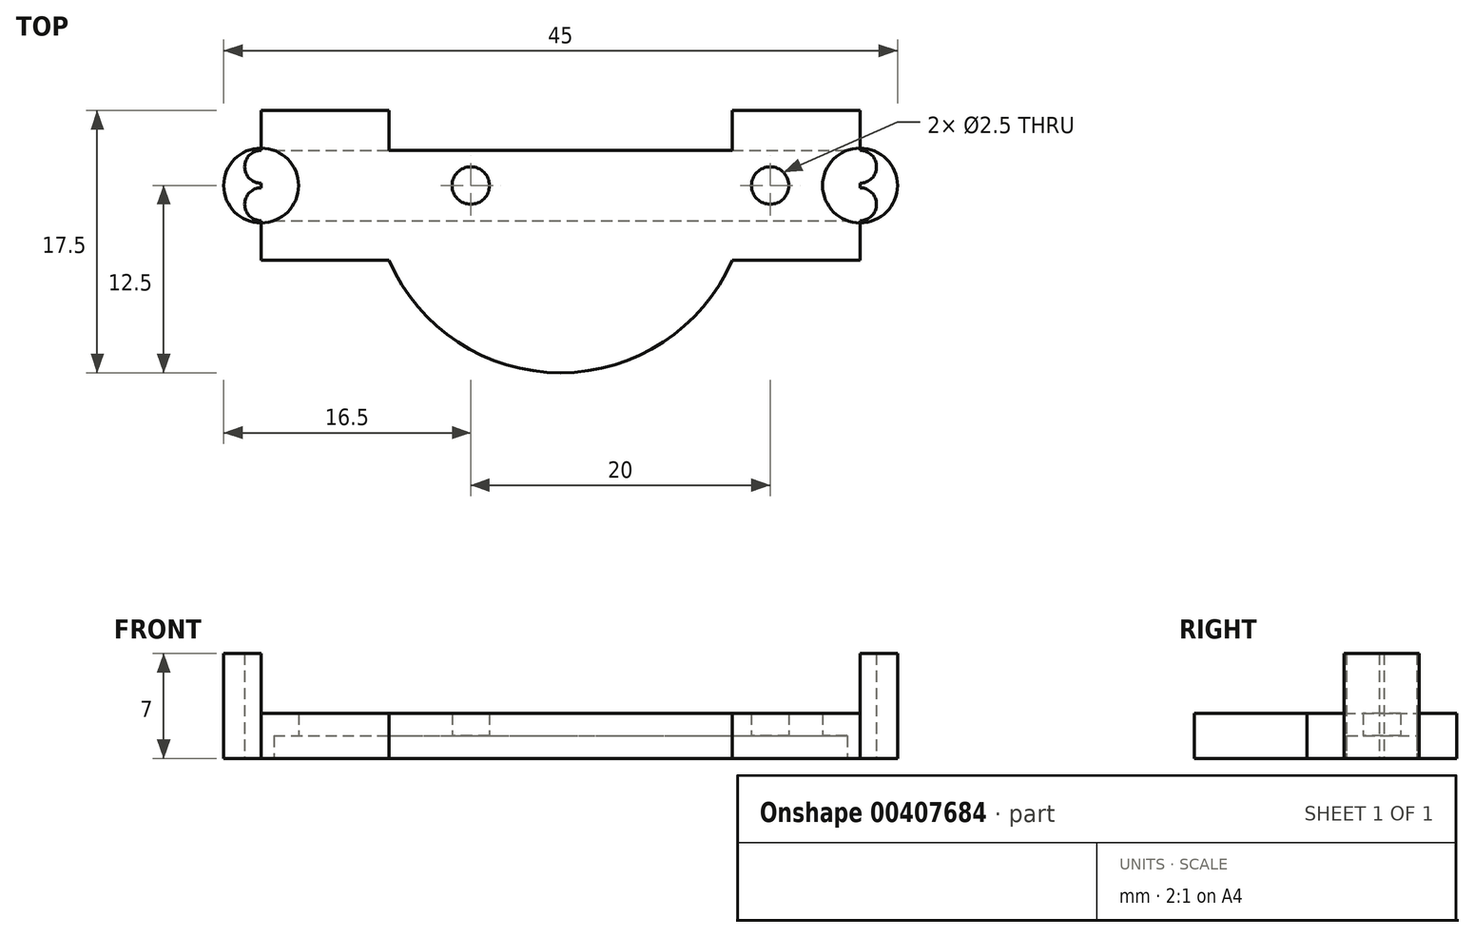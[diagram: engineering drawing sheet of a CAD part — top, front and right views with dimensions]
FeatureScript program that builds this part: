
annotation { "Feature Type Name" : "Feature", "Feature Type Description" : "" }
export const myFeature = defineFeature(function(context is Context, id is Id, definition is map)
    precondition{}
    {
        {
            var Q0;
            Q0=qCreatedBy(makeId("Top.planeOp"),FACE);
            var sketch = newSketch(context, id + "F0", { "sketchPlane" : qUnion([Q0])});
            skCircle(sketch, "E0", {"center": v(0, 0) * mm, "radius": 12.5 * mm});
            skCircle(sketch, "E1", {"center": v(-20, 0) * mm, "radius": 5 * mm});
            skCircle(sketch, "E2", {"center": v(20, 0) * mm, "radius": 5 * mm});
            skLineSegment(sketch, "E3.bottom", {"start": v(-20, 5) * mm, "end": v(-11.46, 5) * mm});
            skLineSegment(sketch, "E3.top", {"start": v(-20, -5) * mm, "end": v(-11.46, -5) * mm});
            skLineSegment(sketch, "E3.left", {"start": v(-20, 5) * mm, "end": v(-20, -5) * mm});
            skLineSegment(sketch, "E3.right", {"start": v(-11.46, 5) * mm, "end": v(-11.46, -5) * mm});
            skLineSegment(sketch, "E4.bottom", {"start": v(20, 5) * mm, "end": v(11.46, 5) * mm});
            skLineSegment(sketch, "E4.top", {"start": v(20, -5) * mm, "end": v(11.46, -5) * mm});
            skLineSegment(sketch, "E4.left", {"start": v(20, 5) * mm, "end": v(20, -5) * mm});
            skLineSegment(sketch, "E4.right", {"start": v(11.46, 5) * mm, "end": v(11.46, -5) * mm});
            skCircle(sketch, "E5", {"center": v(-20, -1.25) * mm, "radius": 1.1 * mm});
            skCircle(sketch, "E6", {"center": v(0, 0) * mm, "radius": 11.5 * mm});
            skPoint(sketch, "E7.firstSnap0", {"position": v(0, -2.27) * mm});
            skCircle(sketch, "E8", {"center": v(-6, 0) * mm, "radius": 1.25 * mm});
            skCircle(sketch, "E9", {"center": v(14, 0) * mm, "radius": 1.25 * mm});
            skCircle(sketch, "E10", {"center": v(-20, 1.25) * mm, "radius": 1.1 * mm});
            skCircle(sketch, "E11", {"center": v(20, -1.25) * mm, "radius": 1.1 * mm});
            skCircle(sketch, "E12", {"center": v(20, 1.25) * mm, "radius": 1.1 * mm});
            skLineSegment(sketch, "E13.bottom", {"start": v(-20, 2.35) * mm, "end": v(20, 2.35) * mm});
            skLineSegment(sketch, "E13.top", {"start": v(-20, -2.35) * mm, "end": v(20, -2.35) * mm});
            skLineSegment(sketch, "E13.left", {"start": v(-20, 2.35) * mm, "end": v(-20, -2.35) * mm});
            skLineSegment(sketch, "E13.right", {"start": v(20, 2.35) * mm, "end": v(20, -2.35) * mm});
            skCircle(sketch, "E14", {"center": v(-20, 0) * mm, "radius": 2.5 * mm});
            skCircle(sketch, "E15", {"center": v(20, 0) * mm, "radius": 2.5 * mm});
            skSolve(sketch);
        }
        {
            var Q0;
            {var subQ1=sQuery(id+"F0.wireOp",EDGE,"E13.bottom");var subQ5=sQuery(id+"F0.wireOp",EDGE,"E1");var subQ6=makeQuery(id+"F0.imprint","INTERSECT",VERTEX,{"derivedFrom":[subQ5,subQ1]});Q0=makeQuery(id+"F0.imprint","IMPRINT",FACE,{"disambiguationData":[TD([[makeQuery(id+"F0.imprint","IMPRINT",EDGE,{"disambiguationData":[TD([[subQ6,1.0]])],"derivedFrom":subQ5}),1.0]])]});}
            var Q1;
            {var subQ1=sQuery(id+"F0.wireOp",EDGE,"E1");var subQ3=sQuery(id+"F0.wireOp",EDGE,"E13.top");var subQ4=makeQuery(id+"F0.imprint","INTERSECT",VERTEX,{"derivedFrom":[subQ1,subQ3]});Q1=makeQuery(id+"F0.imprint","IMPRINT",FACE,{"disambiguationData":[TD([[makeQuery(id+"F0.imprint","IMPRINT",EDGE,{"disambiguationData":[TD([[subQ4,1.0]])],"derivedFrom":subQ1}),1.0]])]});}
            var Q2;
            {var subQ1=sQuery(id+"F0.wireOp",EDGE,"E1");var subQ3=sQuery(id+"F0.wireOp",EDGE,"E13.bottom");var subQ4=makeQuery(id+"F0.imprint","INTERSECT",VERTEX,{"derivedFrom":[subQ1,subQ3]});Q2=makeQuery(id+"F0.imprint","IMPRINT",FACE,{"disambiguationData":[TD([[makeQuery(id+"F0.imprint","IMPRINT",EDGE,{"disambiguationData":[TD([[subQ4,-1.0]])],"derivedFrom":subQ1}),1.0]])]});}
            var Q3;
            {var subQ3=sQuery(id+"F0.wireOp",EDGE,"E13.left");var subQ6=sQuery(id+"F0.wireOp",EDGE,"E5");var subQ8=makeQuery(id+"F0.imprint","INTERSECT",VERTEX,{"derivedFrom":[subQ6,subQ3]});Q3=makeQuery(id+"F0.imprint","IMPRINT",FACE,{"disambiguationData":[TD([[makeQuery(id+"F0.imprint","IMPRINT",EDGE,{"disambiguationData":[TD([[subQ8,1.0]])],"derivedFrom":subQ3}),-1.0]])]});}
            var Q4;
            {var subQ0=sQuery(id+"F0.wireOp",EDGE,"E3.bottom");Q4=makeQuery(id+"F0.imprint","IMPRINT",FACE,{"disambiguationData":[TD([[makeQuery(id+"F0.imprint","IMPRINT",EDGE,{"derivedFrom":subQ0}),-1.0]])]});}
            var Q5;
            {var subQ0=sQuery(id+"F0.wireOp",EDGE,"E3.top");Q5=makeQuery(id+"F0.imprint","IMPRINT",FACE,{"disambiguationData":[TD([[makeQuery(id+"F0.imprint","IMPRINT",EDGE,{"derivedFrom":subQ0}),1.0]])]});}
            var Q6;
            {var subQ0=sQuery(id+"F0.wireOp",EDGE,"E13.bottom");var subQ1=sQuery(id+"F0.wireOp",EDGE,"E0");var subQ2=makeQuery(id+"F0.imprint","INTERSECT",VERTEX,{"disambiguationData":[OD(1.0)],"derivedFrom":[subQ1,subQ0]});Q6=makeQuery(id+"F0.imprint","IMPRINT",FACE,{"disambiguationData":[TD([[makeQuery(id+"F0.imprint","IMPRINT",EDGE,{"disambiguationData":[TD([[subQ2,-1.0]])],"derivedFrom":subQ1}),-1.0]])]});}
            var Q7;
            {var subQ1=sQuery(id+"F0.wireOp",EDGE,"E0");var subQ3=sQuery(id+"F0.wireOp",EDGE,"E13.bottom");var subQ4=makeQuery(id+"F0.imprint","INTERSECT",VERTEX,{"disambiguationData":[OD(1.0)],"derivedFrom":[subQ1,subQ3]});Q7=makeQuery(id+"F0.imprint","IMPRINT",FACE,{"disambiguationData":[TD([[makeQuery(id+"F0.imprint","IMPRINT",EDGE,{"disambiguationData":[TD([[subQ4,-1.0]])],"derivedFrom":subQ3}),1.0]])]});}
            var Q8;
            {var subQ4=sQuery(id+"F0.wireOp",EDGE,"E13.bottom");var subQ6=sQuery(id+"F0.wireOp",EDGE,"E0");var subQ7=makeQuery(id+"F0.imprint","INTERSECT",VERTEX,{"disambiguationData":[OD(1.0)],"derivedFrom":[subQ6,subQ4]});Q8=makeQuery(id+"F0.imprint","IMPRINT",FACE,{"disambiguationData":[TD([[makeQuery(id+"F0.imprint","IMPRINT",EDGE,{"disambiguationData":[TD([[subQ7,-1.0]])],"derivedFrom":subQ6}),1.0]])]});}
            var Q9;
            {var subQ1=sQuery(id+"F0.wireOp",EDGE,"E0");var subQ3=sQuery(id+"F0.wireOp",EDGE,"E13.top");var subQ4=makeQuery(id+"F0.imprint","INTERSECT",VERTEX,{"disambiguationData":[OD(0.0)],"derivedFrom":[subQ1,subQ3]});Q9=makeQuery(id+"F0.imprint","IMPRINT",FACE,{"disambiguationData":[TD([[makeQuery(id+"F0.imprint","IMPRINT",EDGE,{"disambiguationData":[TD([[subQ4,-1.0]])],"derivedFrom":subQ3}),-1.0]])]});}
            var Q10;
            {var subQ0=sQuery(id+"F0.wireOp",EDGE,"E13.bottom");var subQ1=sQuery(id+"F0.wireOp",EDGE,"E3.right");var subQ2=makeQuery(id+"F0.imprint","INTERSECT",VERTEX,{"derivedFrom":[subQ1,subQ0]});Q10=makeQuery(id+"F0.imprint","IMPRINT",FACE,{"disambiguationData":[TD([[makeQuery(id+"F0.imprint","IMPRINT",EDGE,{"disambiguationData":[TD([[subQ2,-1.0]])],"derivedFrom":subQ1}),1.0]])]});}
            var Q11;
            {var subQ0=sQuery(id+"F0.wireOp",EDGE,"E6");var subQ1=sQuery(id+"F0.wireOp",EDGE,"E3.right");var subQ2=makeQuery(id+"F0.imprint","INTERSECT",VERTEX,{"disambiguationData":[OD(1.0)],"derivedFrom":[subQ1,subQ0]});Q11=makeQuery(id+"F0.imprint","IMPRINT",FACE,{"disambiguationData":[TD([[makeQuery(id+"F0.imprint","IMPRINT",EDGE,{"disambiguationData":[TD([[subQ2,-1.0]])],"derivedFrom":subQ1}),1.0]])]});}
            var Q12;
            {var subQ0=sQuery(id+"F0.wireOp",EDGE,"E13.top");var subQ1=sQuery(id+"F0.wireOp",EDGE,"E6");var subQ2=makeQuery(id+"F0.imprint","INTERSECT",VERTEX,{"disambiguationData":[OD(0.0)],"derivedFrom":[subQ1,subQ0]});Q12=makeQuery(id+"F0.imprint","IMPRINT",FACE,{"disambiguationData":[TD([[makeQuery(id+"F0.imprint","IMPRINT",EDGE,{"disambiguationData":[TD([[subQ2,-1.0]])],"derivedFrom":subQ1}),-1.0]])]});}
            var Q13;
            {var subQ0=sQuery(id+"F0.wireOp",EDGE,"E13.bottom");var subQ1=sQuery(id+"F0.wireOp",EDGE,"E6");var subQ2=makeQuery(id+"F0.imprint","INTERSECT",VERTEX,{"disambiguationData":[OD(0.0)],"derivedFrom":[subQ1,subQ0]});Q13=makeQuery(id+"F0.imprint","IMPRINT",FACE,{"disambiguationData":[TD([[makeQuery(id+"F0.imprint","IMPRINT",EDGE,{"disambiguationData":[TD([[subQ2,-1.0]])],"derivedFrom":subQ1}),-1.0]])]});}
            var Q14;
            {var subQ0=sQuery(id+"F0.wireOp",EDGE,"E13.bottom");var subQ1=sQuery(id+"F0.wireOp",EDGE,"E6");var subQ2=makeQuery(id+"F0.imprint","INTERSECT",VERTEX,{"disambiguationData":[OD(0.0)],"derivedFrom":[subQ1,subQ0]});Q14=makeQuery(id+"F0.imprint","IMPRINT",FACE,{"disambiguationData":[TD([[makeQuery(id+"F0.imprint","IMPRINT",EDGE,{"disambiguationData":[TD([[subQ2,-1.0]])],"derivedFrom":subQ1}),1.0]])]});}
            var Q15;
            {var subQ0=sQuery(id+"F0.wireOp",EDGE,"E13.top");var subQ1=sQuery(id+"F0.wireOp",EDGE,"E6");var subQ2=makeQuery(id+"F0.imprint","INTERSECT",VERTEX,{"disambiguationData":[OD(0.0)],"derivedFrom":[subQ1,subQ0]});Q15=makeQuery(id+"F0.imprint","IMPRINT",FACE,{"disambiguationData":[TD([[makeQuery(id+"F0.imprint","IMPRINT",EDGE,{"disambiguationData":[TD([[subQ2,-1.0]])],"derivedFrom":subQ1}),1.0]])]});}
            var Q16;
            Q16=makeQuery(id+"F0.imprint","IMPRINT",FACE,{"disambiguationData":[TD([[makeQuery(id+"F0.imprint","IMPRINT",EDGE,{"derivedFrom":sQuery(id+"F0.wireOp",EDGE,"E8")}),-1.0]])]});
            var Q17;
            {var subQ0=sQuery(id+"F0.wireOp",EDGE,"E13.bottom");var subQ1=sQuery(id+"F0.wireOp",EDGE,"E4.right");var subQ2=makeQuery(id+"F0.imprint","INTERSECT",VERTEX,{"derivedFrom":[subQ1,subQ0]});Q17=makeQuery(id+"F0.imprint","IMPRINT",FACE,{"disambiguationData":[TD([[makeQuery(id+"F0.imprint","IMPRINT",EDGE,{"disambiguationData":[TD([[subQ2,-1.0]])],"derivedFrom":subQ1}),-1.0]])]});}
            var Q18;
            {var subQ0=sQuery(id+"F0.wireOp",EDGE,"E6");var subQ1=sQuery(id+"F0.wireOp",EDGE,"E4.right");var subQ2=makeQuery(id+"F0.imprint","INTERSECT",VERTEX,{"disambiguationData":[OD(1.0)],"derivedFrom":[subQ1,subQ0]});Q18=makeQuery(id+"F0.imprint","IMPRINT",FACE,{"disambiguationData":[TD([[makeQuery(id+"F0.imprint","IMPRINT",EDGE,{"disambiguationData":[TD([[subQ2,-1.0]])],"derivedFrom":subQ1}),-1.0]])]});}
            var Q19;
            {var subQ1=sQuery(id+"F0.wireOp",EDGE,"E0");var subQ3=sQuery(id+"F0.wireOp",EDGE,"E13.top");var subQ4=makeQuery(id+"F0.imprint","INTERSECT",VERTEX,{"disambiguationData":[OD(1.0)],"derivedFrom":[subQ1,subQ3]});Q19=makeQuery(id+"F0.imprint","IMPRINT",FACE,{"disambiguationData":[TD([[makeQuery(id+"F0.imprint","IMPRINT",EDGE,{"disambiguationData":[TD([[subQ4,1.0]])],"derivedFrom":subQ3}),-1.0]])]});}
            var Q20;
            {var subQ1=sQuery(id+"F0.wireOp",EDGE,"E0");var subQ3=sQuery(id+"F0.wireOp",EDGE,"E13.bottom");var subQ4=makeQuery(id+"F0.imprint","INTERSECT",VERTEX,{"disambiguationData":[OD(0.0)],"derivedFrom":[subQ1,subQ3]});Q20=makeQuery(id+"F0.imprint","IMPRINT",FACE,{"disambiguationData":[TD([[makeQuery(id+"F0.imprint","IMPRINT",EDGE,{"disambiguationData":[TD([[subQ4,1.0]])],"derivedFrom":subQ3}),1.0]])]});}
            var Q21;
            {var subQ6=sQuery(id+"F0.wireOp",EDGE,"E13.bottom");var subQ8=sQuery(id+"F0.wireOp",EDGE,"E0");var subQ9=makeQuery(id+"F0.imprint","INTERSECT",VERTEX,{"disambiguationData":[OD(0.0)],"derivedFrom":[subQ8,subQ6]});Q21=makeQuery(id+"F0.imprint","IMPRINT",FACE,{"disambiguationData":[TD([[makeQuery(id+"F0.imprint","IMPRINT",EDGE,{"disambiguationData":[TD([[subQ9,1.0]])],"derivedFrom":subQ8}),1.0]])]});}
            var Q22;
            {var subQ0=sQuery(id+"F0.wireOp",EDGE,"E4.bottom");Q22=makeQuery(id+"F0.imprint","IMPRINT",FACE,{"disambiguationData":[TD([[makeQuery(id+"F0.imprint","IMPRINT",EDGE,{"derivedFrom":subQ0}),1.0]])]});}
            var Q23;
            {var subQ0=sQuery(id+"F0.wireOp",EDGE,"E4.top");Q23=makeQuery(id+"F0.imprint","IMPRINT",FACE,{"disambiguationData":[TD([[makeQuery(id+"F0.imprint","IMPRINT",EDGE,{"derivedFrom":subQ0}),-1.0]])]});}
            var Q24;
            Q24=makeQuery(id+"F0.imprint","IMPRINT",FACE,{"disambiguationData":[TD([[makeQuery(id+"F0.imprint","IMPRINT",EDGE,{"derivedFrom":sQuery(id+"F0.wireOp",EDGE,"E9")}),-1.0]])]});
            var Q25;
            {var subQ1=sQuery(id+"F0.wireOp",EDGE,"E2");var subQ3=sQuery(id+"F0.wireOp",EDGE,"E13.bottom");var subQ4=makeQuery(id+"F0.imprint","INTERSECT",VERTEX,{"derivedFrom":[subQ1,subQ3]});Q25=makeQuery(id+"F0.imprint","IMPRINT",FACE,{"disambiguationData":[TD([[makeQuery(id+"F0.imprint","IMPRINT",EDGE,{"disambiguationData":[TD([[subQ4,1.0]])],"derivedFrom":subQ1}),1.0]])]});}
            var Q26;
            {var subQ0=sQuery(id+"F0.wireOp",EDGE,"E13.right");var subQ1=sQuery(id+"F0.wireOp",EDGE,"E11");var subQ4=makeQuery(id+"F0.imprint","INTERSECT",VERTEX,{"derivedFrom":[subQ1,subQ0]});Q26=makeQuery(id+"F0.imprint","IMPRINT",FACE,{"disambiguationData":[TD([[makeQuery(id+"F0.imprint","IMPRINT",EDGE,{"disambiguationData":[TD([[subQ4,1.0]])],"derivedFrom":subQ0}),1.0]])]});}
            var Q27;
            {var subQ1=sQuery(id+"F0.wireOp",EDGE,"E2");var subQ3=sQuery(id+"F0.wireOp",EDGE,"E13.top");var subQ4=makeQuery(id+"F0.imprint","INTERSECT",VERTEX,{"derivedFrom":[subQ1,subQ3]});Q27=makeQuery(id+"F0.imprint","IMPRINT",FACE,{"disambiguationData":[TD([[makeQuery(id+"F0.imprint","IMPRINT",EDGE,{"disambiguationData":[TD([[subQ4,-1.0]])],"derivedFrom":subQ1}),1.0]])]});}
            var Q28;
            {var subQ1=sQuery(id+"F0.wireOp",EDGE,"E13.bottom");var subQ5=sQuery(id+"F0.wireOp",EDGE,"E2");var subQ6=makeQuery(id+"F0.imprint","INTERSECT",VERTEX,{"derivedFrom":[subQ5,subQ1]});Q28=makeQuery(id+"F0.imprint","IMPRINT",FACE,{"disambiguationData":[TD([[makeQuery(id+"F0.imprint","IMPRINT",EDGE,{"disambiguationData":[TD([[subQ6,-1.0]])],"derivedFrom":subQ5}),1.0]])]});}
            var Q29;
            {var subQ0=sQuery(id+"F0.wireOp",EDGE,"E6");var subQ1=sQuery(id+"F0.wireOp",EDGE,"E3.right");var subQ2=makeQuery(id+"F0.imprint","INTERSECT",VERTEX,{"disambiguationData":[OD(0.0)],"derivedFrom":[subQ1,subQ0]});Q29=makeQuery(id+"F0.imprint","IMPRINT",FACE,{"disambiguationData":[TD([[makeQuery(id+"F0.imprint","IMPRINT",EDGE,{"disambiguationData":[TD([[subQ2,-1.0]])],"derivedFrom":subQ1}),-1.0]])]});}
            var Q30;
            {var subQ0=sQuery(id+"F0.wireOp",EDGE,"E6");var subQ1=sQuery(id+"F0.wireOp",EDGE,"E4.right");var subQ2=makeQuery(id+"F0.imprint","INTERSECT",VERTEX,{"disambiguationData":[OD(0.0)],"derivedFrom":[subQ1,subQ0]});Q30=makeQuery(id+"F0.imprint","IMPRINT",FACE,{"disambiguationData":[TD([[makeQuery(id+"F0.imprint","IMPRINT",EDGE,{"disambiguationData":[TD([[subQ2,-1.0]])],"derivedFrom":subQ1}),1.0]])]});}
            var Q31;
            {var subQ0=sQuery(id+"F0.wireOp",EDGE,"E4.left");var subQ4=sQuery(id+"F0.wireOp",EDGE,"E15");var subQ5=makeQuery(id+"F0.imprint","INTERSECT",VERTEX,{"disambiguationData":[OD(0.0)],"derivedFrom":[subQ0,subQ4]});Q31=makeQuery(id+"F0.imprint","IMPRINT",FACE,{"disambiguationData":[TD([[makeQuery(id+"F0.imprint","IMPRINT",EDGE,{"disambiguationData":[TD([[subQ5,1.0]])],"derivedFrom":subQ4}),-1.0]])]});}
            var Q32;
            {var subQ0=sQuery(id+"F0.wireOp",EDGE,"E3.left");var subQ4=sQuery(id+"F0.wireOp",EDGE,"E14");var subQ5=makeQuery(id+"F0.imprint","INTERSECT",VERTEX,{"disambiguationData":[OD(0.0)],"derivedFrom":[subQ0,subQ4]});Q32=makeQuery(id+"F0.imprint","IMPRINT",FACE,{"disambiguationData":[TD([[makeQuery(id+"F0.imprint","IMPRINT",EDGE,{"disambiguationData":[TD([[subQ5,-1.0]])],"derivedFrom":subQ4}),-1.0]])]});}
            var Q33;
            {var subQ0=sQuery(id+"F0.wireOp",EDGE,"E13.left");var subQ2=sQuery(id+"F0.wireOp",EDGE,"E5");var subQ12=makeQuery(id+"F0.imprint","INTERSECT",VERTEX,{"derivedFrom":[subQ2,subQ0]});Q33=makeQuery(id+"F0.imprint","IMPRINT",FACE,{"disambiguationData":[TD([[makeQuery(id+"F0.imprint","IMPRINT",EDGE,{"disambiguationData":[TD([[subQ12,1.0]])],"derivedFrom":subQ0}),1.0]])]});}
            var Q34;
            {var subQ1=sQuery(id+"F0.wireOp",EDGE,"E3.left");var subQ3=sQuery(id+"F0.wireOp",EDGE,"E14");var subQ4=makeQuery(id+"F0.imprint","INTERSECT",VERTEX,{"disambiguationData":[OD(1.0)],"derivedFrom":[subQ1,subQ3]});Q34=makeQuery(id+"F0.imprint","IMPRINT",FACE,{"disambiguationData":[TD([[makeQuery(id+"F0.imprint","IMPRINT",EDGE,{"disambiguationData":[TD([[subQ4,-1.0]])],"derivedFrom":subQ3}),1.0]])]});}
            var Q35;
            {var subQ1=sQuery(id+"F0.wireOp",EDGE,"E3.left");var subQ3=sQuery(id+"F0.wireOp",EDGE,"E14");var subQ4=makeQuery(id+"F0.imprint","INTERSECT",VERTEX,{"disambiguationData":[OD(0.0)],"derivedFrom":[subQ1,subQ3]});Q35=makeQuery(id+"F0.imprint","IMPRINT",FACE,{"disambiguationData":[TD([[makeQuery(id+"F0.imprint","IMPRINT",EDGE,{"disambiguationData":[TD([[subQ4,1.0]])],"derivedFrom":subQ3}),1.0]])]});}
            var Q36;
            {var subQ0=sQuery(id+"F0.wireOp",EDGE,"E13.right");var subQ8=sQuery(id+"F0.wireOp",EDGE,"E11");var subQ12=makeQuery(id+"F0.imprint","INTERSECT",VERTEX,{"derivedFrom":[subQ8,subQ0]});Q36=makeQuery(id+"F0.imprint","IMPRINT",FACE,{"disambiguationData":[TD([[makeQuery(id+"F0.imprint","IMPRINT",EDGE,{"disambiguationData":[TD([[subQ12,1.0]])],"derivedFrom":subQ0}),-1.0]])]});}
            var Q37;
            {var subQ1=sQuery(id+"F0.wireOp",EDGE,"E4.left");var subQ3=sQuery(id+"F0.wireOp",EDGE,"E15");var subQ4=makeQuery(id+"F0.imprint","INTERSECT",VERTEX,{"disambiguationData":[OD(0.0)],"derivedFrom":[subQ1,subQ3]});Q37=makeQuery(id+"F0.imprint","IMPRINT",FACE,{"disambiguationData":[TD([[makeQuery(id+"F0.imprint","IMPRINT",EDGE,{"disambiguationData":[TD([[subQ4,-1.0]])],"derivedFrom":subQ3}),1.0]])]});}
            var Q38;
            {var subQ1=sQuery(id+"F0.wireOp",EDGE,"E4.left");var subQ3=sQuery(id+"F0.wireOp",EDGE,"E15");var subQ4=makeQuery(id+"F0.imprint","INTERSECT",VERTEX,{"disambiguationData":[OD(1.0)],"derivedFrom":[subQ1,subQ3]});Q38=makeQuery(id+"F0.imprint","IMPRINT",FACE,{"disambiguationData":[TD([[makeQuery(id+"F0.imprint","IMPRINT",EDGE,{"disambiguationData":[TD([[subQ4,1.0]])],"derivedFrom":subQ3}),1.0]])]});}
            extrude(context, id + "F1", {"entities" : qUnion([Q0, Q1, Q2, Q3, Q4, Q5, Q6, Q7, Q8, Q9, Q10, Q11, Q12, Q13, Q14, Q15, Q16, Q17, Q18, Q19, Q20, Q21, Q22, Q23, Q24, Q25, Q26, Q27, Q28, Q29, Q30, Q31, Q32, Q33, Q34, Q35, Q36, Q37, Q38]), "depth" : 3 * mm});
        }
        {
            var Q0;
            {var subQ0=sQuery(id+"F0.wireOp",EDGE,"E13.left");var subQ2=sQuery(id+"F0.wireOp",EDGE,"E5");var subQ12=makeQuery(id+"F0.imprint","INTERSECT",VERTEX,{"derivedFrom":[subQ2,subQ0]});Q0=makeQuery(id+"F0.imprint","IMPRINT",FACE,{"disambiguationData":[TD([[makeQuery(id+"F0.imprint","IMPRINT",EDGE,{"disambiguationData":[TD([[subQ12,1.0]])],"derivedFrom":subQ0}),1.0]])]});}
            var Q1;
            {var subQ1=sQuery(id+"F0.wireOp",EDGE,"E3.left");var subQ3=sQuery(id+"F0.wireOp",EDGE,"E14");var subQ4=makeQuery(id+"F0.imprint","INTERSECT",VERTEX,{"disambiguationData":[OD(1.0)],"derivedFrom":[subQ1,subQ3]});Q1=makeQuery(id+"F0.imprint","IMPRINT",FACE,{"disambiguationData":[TD([[makeQuery(id+"F0.imprint","IMPRINT",EDGE,{"disambiguationData":[TD([[subQ4,-1.0]])],"derivedFrom":subQ3}),1.0]])]});}
            var Q2;
            {var subQ0=sQuery(id+"F0.wireOp",EDGE,"E13.left");var subQ5=sQuery(id+"F0.wireOp",EDGE,"E5");var subQ7=makeQuery(id+"F0.imprint","INTERSECT",VERTEX,{"derivedFrom":[subQ5,subQ0]});Q2=makeQuery(id+"F0.imprint","IMPRINT",FACE,{"disambiguationData":[TD([[makeQuery(id+"F0.imprint","IMPRINT",EDGE,{"disambiguationData":[TD([[subQ7,1.0]])],"derivedFrom":subQ0}),-1.0]])]});}
            var Q3;
            {var subQ1=sQuery(id+"F0.wireOp",EDGE,"E3.left");var subQ3=sQuery(id+"F0.wireOp",EDGE,"E14");var subQ4=makeQuery(id+"F0.imprint","INTERSECT",VERTEX,{"disambiguationData":[OD(0.0)],"derivedFrom":[subQ1,subQ3]});Q3=makeQuery(id+"F0.imprint","IMPRINT",FACE,{"disambiguationData":[TD([[makeQuery(id+"F0.imprint","IMPRINT",EDGE,{"disambiguationData":[TD([[subQ4,1.0]])],"derivedFrom":subQ3}),1.0]])]});}
            var Q4;
            {var subQ1=sQuery(id+"F0.wireOp",EDGE,"E4.left");var subQ3=sQuery(id+"F0.wireOp",EDGE,"E15");var subQ4=makeQuery(id+"F0.imprint","INTERSECT",VERTEX,{"disambiguationData":[OD(1.0)],"derivedFrom":[subQ1,subQ3]});Q4=makeQuery(id+"F0.imprint","IMPRINT",FACE,{"disambiguationData":[TD([[makeQuery(id+"F0.imprint","IMPRINT",EDGE,{"disambiguationData":[TD([[subQ4,1.0]])],"derivedFrom":subQ3}),1.0]])]});}
            var Q5;
            {var subQ0=sQuery(id+"F0.wireOp",EDGE,"E13.right");var subQ8=sQuery(id+"F0.wireOp",EDGE,"E11");var subQ12=makeQuery(id+"F0.imprint","INTERSECT",VERTEX,{"derivedFrom":[subQ8,subQ0]});Q5=makeQuery(id+"F0.imprint","IMPRINT",FACE,{"disambiguationData":[TD([[makeQuery(id+"F0.imprint","IMPRINT",EDGE,{"disambiguationData":[TD([[subQ12,1.0]])],"derivedFrom":subQ0}),-1.0]])]});}
            var Q6;
            {var subQ0=sQuery(id+"F0.wireOp",EDGE,"E13.right");var subQ1=sQuery(id+"F0.wireOp",EDGE,"E11");var subQ4=makeQuery(id+"F0.imprint","INTERSECT",VERTEX,{"derivedFrom":[subQ1,subQ0]});Q6=makeQuery(id+"F0.imprint","IMPRINT",FACE,{"disambiguationData":[TD([[makeQuery(id+"F0.imprint","IMPRINT",EDGE,{"disambiguationData":[TD([[subQ4,1.0]])],"derivedFrom":subQ0}),1.0]])]});}
            var Q7;
            {var subQ1=sQuery(id+"F0.wireOp",EDGE,"E4.left");var subQ3=sQuery(id+"F0.wireOp",EDGE,"E15");var subQ4=makeQuery(id+"F0.imprint","INTERSECT",VERTEX,{"disambiguationData":[OD(0.0)],"derivedFrom":[subQ1,subQ3]});Q7=makeQuery(id+"F0.imprint","IMPRINT",FACE,{"disambiguationData":[TD([[makeQuery(id+"F0.imprint","IMPRINT",EDGE,{"disambiguationData":[TD([[subQ4,-1.0]])],"derivedFrom":subQ3}),1.0]])]});}
            extrude(context, id + "F2", {"entities" : qUnion([Q0, Q1, Q2, Q3, Q4, Q5, Q6, Q7]), "operationType" : NewBodyOperationType.ADD, "depth" : 7 * mm});
        }
        {
            var Q0;
            {var subQ1=sQuery(id+"F0.wireOp",EDGE,"E13.bottom");var subQ5=sQuery(id+"F0.wireOp",EDGE,"ZJ16MpWJ-6GMt-Xyfp-zZQC-vbQ30tvc5Ikp");var subQ6=makeQuery(id+"F0.imprint","INTERSECT",VERTEX,{"derivedFrom":[subQ5,subQ1]});Q0=makeQuery(id+"F0.imprint","IMPRINT",FACE,{"disambiguationData":[TD([[makeQuery(id+"F0.imprint","IMPRINT",EDGE,{"disambiguationData":[TD([[subQ6,1.0]])],"derivedFrom":subQ5}),1.0]])]});}
            var Q1;
            {var subQ0=sQuery(id+"F0.wireOp",EDGE,"E13.bottom");var subQ1=sQuery(id+"F0.wireOp",EDGE,"E1");var subQ2=makeQuery(id+"F0.imprint","INTERSECT",VERTEX,{"derivedFrom":[subQ1,subQ0]});Q1=makeQuery(id+"F0.imprint","IMPRINT",FACE,{"disambiguationData":[TD([[makeQuery(id+"F0.imprint","IMPRINT",EDGE,{"disambiguationData":[TD([[subQ2,1.0]])],"derivedFrom":subQ1}),1.0]])]});}
            var Q2;
            {var subQ0=sQuery(id+"F0.wireOp",EDGE,"E13.bottom");var subQ1=sQuery(id+"F0.wireOp",EDGE,"E0");var subQ2=makeQuery(id+"F0.imprint","INTERSECT",VERTEX,{"disambiguationData":[OD(1.0)],"derivedFrom":[subQ1,subQ0]});Q2=makeQuery(id+"F0.imprint","IMPRINT",FACE,{"disambiguationData":[TD([[makeQuery(id+"F0.imprint","IMPRINT",EDGE,{"disambiguationData":[TD([[subQ2,-1.0]])],"derivedFrom":subQ1}),-1.0]])]});}
            var Q3;
            {var subQ6=sQuery(id+"F0.wireOp",EDGE,"E13.bottom");var subQ7=sQuery(id+"F0.wireOp",EDGE,"E0");var subQ8=makeQuery(id+"F0.imprint","INTERSECT",VERTEX,{"disambiguationData":[OD(1.0)],"derivedFrom":[subQ7,subQ6]});Q3=makeQuery(id+"F0.imprint","IMPRINT",FACE,{"disambiguationData":[TD([[makeQuery(id+"F0.imprint","IMPRINT",EDGE,{"disambiguationData":[TD([[subQ8,-1.0]])],"derivedFrom":subQ7}),1.0]])]});}
            var Q4;
            {var subQ0=sQuery(id+"F0.wireOp",EDGE,"E13.bottom");var subQ1=sQuery(id+"F0.wireOp",EDGE,"E3.right");var subQ2=makeQuery(id+"F0.imprint","INTERSECT",VERTEX,{"derivedFrom":[subQ1,subQ0]});Q4=makeQuery(id+"F0.imprint","IMPRINT",FACE,{"disambiguationData":[TD([[makeQuery(id+"F0.imprint","IMPRINT",EDGE,{"disambiguationData":[TD([[subQ2,-1.0]])],"derivedFrom":subQ1}),1.0]])]});}
            var Q5;
            {var subQ0=sQuery(id+"F0.wireOp",EDGE,"E6");var subQ1=sQuery(id+"F0.wireOp",EDGE,"E3.right");var subQ2=makeQuery(id+"F0.imprint","INTERSECT",VERTEX,{"disambiguationData":[OD(1.0)],"derivedFrom":[subQ1,subQ0]});Q5=makeQuery(id+"F0.imprint","IMPRINT",FACE,{"disambiguationData":[TD([[makeQuery(id+"F0.imprint","IMPRINT",EDGE,{"disambiguationData":[TD([[subQ2,-1.0]])],"derivedFrom":subQ1}),1.0]])]});}
            var Q6;
            Q6=makeQuery(id+"F0.imprint","IMPRINT",FACE,{"disambiguationData":[TD([[makeQuery(id+"F0.imprint","IMPRINT",EDGE,{"derivedFrom":sQuery(id+"F0.wireOp",EDGE,"E8")}),-1.0]])]});
            var Q7;
            {var subQ0=sQuery(id+"F0.wireOp",EDGE,"E13.bottom");var subQ1=sQuery(id+"F0.wireOp",EDGE,"E4.right");var subQ2=makeQuery(id+"F0.imprint","INTERSECT",VERTEX,{"derivedFrom":[subQ1,subQ0]});Q7=makeQuery(id+"F0.imprint","IMPRINT",FACE,{"disambiguationData":[TD([[makeQuery(id+"F0.imprint","IMPRINT",EDGE,{"disambiguationData":[TD([[subQ2,-1.0]])],"derivedFrom":subQ1}),-1.0]])]});}
            var Q8;
            {var subQ0=sQuery(id+"F0.wireOp",EDGE,"E6");var subQ1=sQuery(id+"F0.wireOp",EDGE,"E4.right");var subQ2=makeQuery(id+"F0.imprint","INTERSECT",VERTEX,{"disambiguationData":[OD(1.0)],"derivedFrom":[subQ1,subQ0]});Q8=makeQuery(id+"F0.imprint","IMPRINT",FACE,{"disambiguationData":[TD([[makeQuery(id+"F0.imprint","IMPRINT",EDGE,{"disambiguationData":[TD([[subQ2,-1.0]])],"derivedFrom":subQ1}),-1.0]])]});}
            var Q9;
            {var subQ6=sQuery(id+"F0.wireOp",EDGE,"E13.bottom");var subQ8=sQuery(id+"F0.wireOp",EDGE,"E0");var subQ9=makeQuery(id+"F0.imprint","INTERSECT",VERTEX,{"disambiguationData":[OD(0.0)],"derivedFrom":[subQ8,subQ6]});Q9=makeQuery(id+"F0.imprint","IMPRINT",FACE,{"disambiguationData":[TD([[makeQuery(id+"F0.imprint","IMPRINT",EDGE,{"disambiguationData":[TD([[subQ9,1.0]])],"derivedFrom":subQ8}),1.0]])]});}
            var Q10;
            Q10=makeQuery(id+"F0.imprint","IMPRINT",FACE,{"disambiguationData":[TD([[makeQuery(id+"F0.imprint","IMPRINT",EDGE,{"derivedFrom":sQuery(id+"F0.wireOp",EDGE,"E9")}),-1.0]])]});
            var Q11;
            {var subQ0=sQuery(id+"F0.wireOp",EDGE,"E13.bottom");var subQ1=sQuery(id+"F0.wireOp",EDGE,"E2");var subQ2=makeQuery(id+"F0.imprint","INTERSECT",VERTEX,{"derivedFrom":[subQ1,subQ0]});Q11=makeQuery(id+"F0.imprint","IMPRINT",FACE,{"disambiguationData":[TD([[makeQuery(id+"F0.imprint","IMPRINT",EDGE,{"disambiguationData":[TD([[subQ2,-1.0]])],"derivedFrom":subQ1}),1.0]])]});}
            var Q12;
            {var subQ1=sQuery(id+"F0.wireOp",EDGE,"E13.bottom");var subQ10=sQuery(id+"F0.wireOp",EDGE,"0F1Torpo-upKr-T72A-I5Kd-2maCx50j9EhH");var subQ11=makeQuery(id+"F0.imprint","INTERSECT",VERTEX,{"derivedFrom":[subQ10,subQ1]});Q12=makeQuery(id+"F0.imprint","IMPRINT",FACE,{"disambiguationData":[TD([[makeQuery(id+"F0.imprint","IMPRINT",EDGE,{"disambiguationData":[TD([[subQ11,-1.0]])],"derivedFrom":subQ10}),1.0]])]});}
            var Q13;
            {var subQ0=sQuery(id+"F0.wireOp",EDGE,"E6");var subQ1=sQuery(id+"F0.wireOp",EDGE,"E4.right");var subQ2=makeQuery(id+"F0.imprint","INTERSECT",VERTEX,{"disambiguationData":[OD(0.0)],"derivedFrom":[subQ1,subQ0]});Q13=makeQuery(id+"F0.imprint","IMPRINT",FACE,{"disambiguationData":[TD([[makeQuery(id+"F0.imprint","IMPRINT",EDGE,{"disambiguationData":[TD([[subQ2,-1.0]])],"derivedFrom":subQ1}),1.0]])]});}
            var Q14;
            {var subQ0=sQuery(id+"F0.wireOp",EDGE,"E6");var subQ1=sQuery(id+"F0.wireOp",EDGE,"E3.right");var subQ2=makeQuery(id+"F0.imprint","INTERSECT",VERTEX,{"disambiguationData":[OD(0.0)],"derivedFrom":[subQ1,subQ0]});Q14=makeQuery(id+"F0.imprint","IMPRINT",FACE,{"disambiguationData":[TD([[makeQuery(id+"F0.imprint","IMPRINT",EDGE,{"disambiguationData":[TD([[subQ2,-1.0]])],"derivedFrom":subQ1}),-1.0]])]});}
            var Q15;
            {var subQ0=sQuery(id+"F0.wireOp",EDGE,"E13.left");var subQ2=sQuery(id+"F0.wireOp",EDGE,"E5");var subQ12=makeQuery(id+"F0.imprint","INTERSECT",VERTEX,{"derivedFrom":[subQ2,subQ0]});Q15=makeQuery(id+"F0.imprint","IMPRINT",FACE,{"disambiguationData":[TD([[makeQuery(id+"F0.imprint","IMPRINT",EDGE,{"disambiguationData":[TD([[subQ12,1.0]])],"derivedFrom":subQ0}),1.0]])]});}
            var Q16;
            {var subQ0=sQuery(id+"F0.wireOp",EDGE,"E13.right");var subQ8=sQuery(id+"F0.wireOp",EDGE,"E11");var subQ12=makeQuery(id+"F0.imprint","INTERSECT",VERTEX,{"derivedFrom":[subQ8,subQ0]});Q16=makeQuery(id+"F0.imprint","IMPRINT",FACE,{"disambiguationData":[TD([[makeQuery(id+"F0.imprint","IMPRINT",EDGE,{"disambiguationData":[TD([[subQ12,1.0]])],"derivedFrom":subQ0}),-1.0]])]});}
            extrude(context, id + "F3", {"entities" : qUnion([Q0, Q1, Q2, Q3, Q4, Q5, Q6, Q7, Q8, Q9, Q10, Q11, Q12, Q13, Q14, Q15, Q16]), "depth" : 1.5 * mm});
        }
        {
            var Q0;
            Q0=makeQuery(id+"F3.opExtrude","SWEPT_BODY",BODY,{"disambiguationData":[OSD([sQuery(id+"F0.wireOp",EDGE,"E5"),sQuery(id+"F0.wireOp",EDGE,"E8"),sQuery(id+"F0.wireOp",EDGE,"E9"),sQuery(id+"F0.wireOp",EDGE,"E10"),sQuery(id+"F0.wireOp",EDGE,"E11"),sQuery(id+"F0.wireOp",EDGE,"E12"),sQuery(id+"F0.wireOp",EDGE,"E13.bottom"),sQuery(id+"F0.wireOp",EDGE,"E13.top"),sQuery(id+"F0.wireOp",EDGE,"E13.left"),sQuery(id+"F0.wireOp",EDGE,"E13.right")])]});
            var Q1;
            Q1=makeQuery(id+"F1.opExtrude","SWEPT_BODY",BODY,{"disambiguationData":[OSD([sQuery(id+"F0.wireOp",EDGE,"E0"),sQuery(id+"F0.wireOp",EDGE,"E1"),sQuery(id+"F0.wireOp",EDGE,"E2"),sQuery(id+"F0.wireOp",EDGE,"E3.bottom"),sQuery(id+"F0.wireOp",EDGE,"E3.top"),sQuery(id+"F0.wireOp",EDGE,"E4.bottom"),sQuery(id+"F0.wireOp",EDGE,"E4.top"),sQuery(id+"F0.wireOp",EDGE,"E5"),sQuery(id+"F0.wireOp",EDGE,"E8"),sQuery(id+"F0.wireOp",EDGE,"E9"),sQuery(id+"F0.wireOp",EDGE,"E10"),sQuery(id+"F0.wireOp",EDGE,"E11"),sQuery(id+"F0.wireOp",EDGE,"E12")])]});
            var Q2;
            Q2=makeQuery(id+"F3.opExtrude","CAP_FACE",FACE,{"disambiguationData":[OSD([sQuery(id+"F0.wireOp",EDGE,"E5"),sQuery(id+"F0.wireOp",EDGE,"E8"),sQuery(id+"F0.wireOp",EDGE,"E9"),sQuery(id+"F0.wireOp",EDGE,"E10"),sQuery(id+"F0.wireOp",EDGE,"E11"),sQuery(id+"F0.wireOp",EDGE,"E12"),sQuery(id+"F0.wireOp",EDGE,"E13.bottom"),sQuery(id+"F0.wireOp",EDGE,"E13.top"),sQuery(id+"F0.wireOp",EDGE,"E13.left"),sQuery(id+"F0.wireOp",EDGE,"E13.right")])],"isStart":true});
            booleanBodies(context, id + "F4", {"operationType" : BooleanOperationType.SUBTRACTION, "tools" : qUnion([Q0]), "targets" : qUnion([Q1]), "entitiesToOffset" : qUnion([Q2]), "reFillet" : true});
        }
    });
